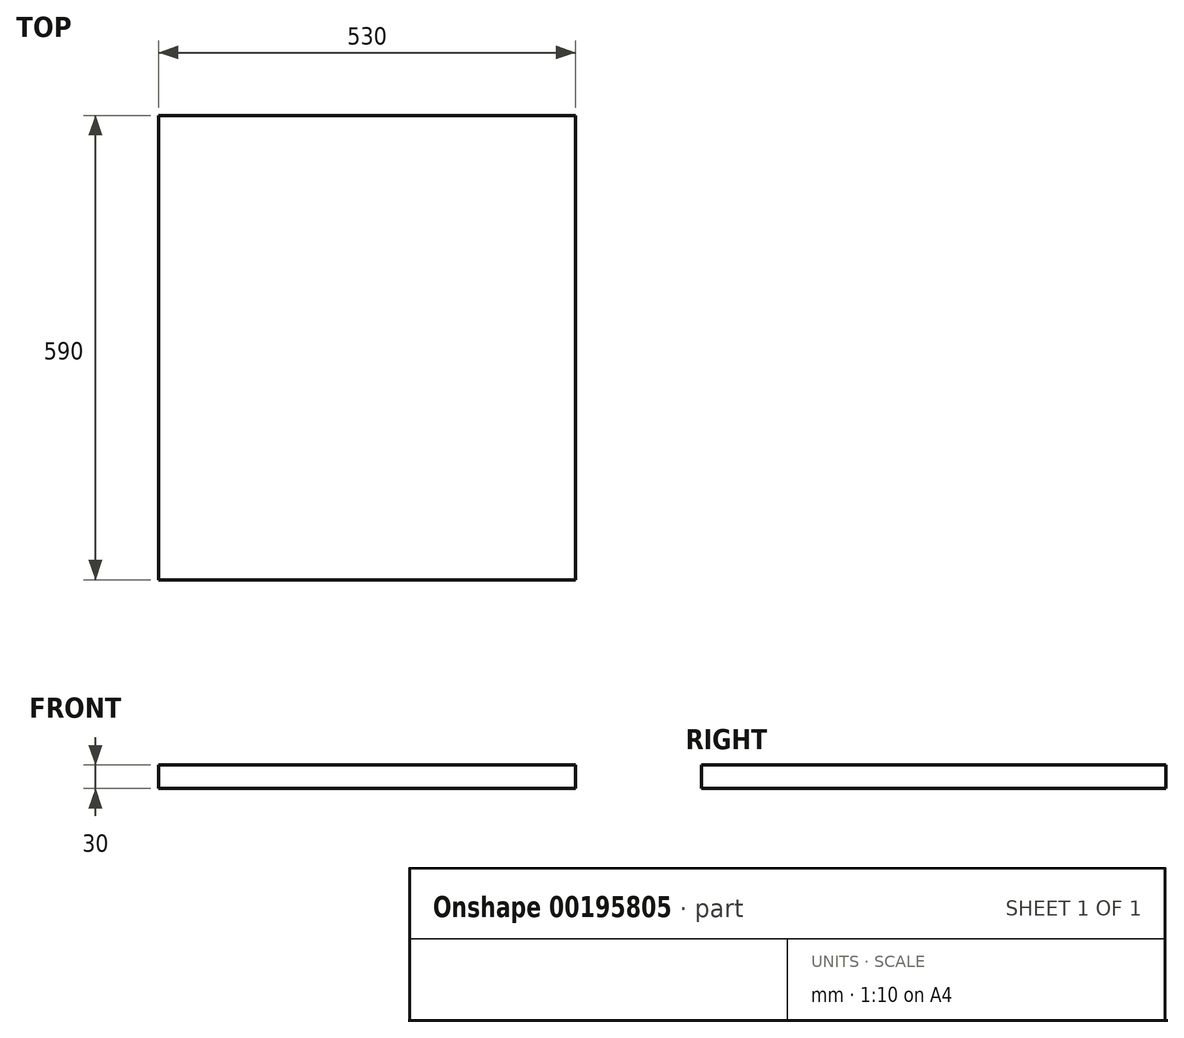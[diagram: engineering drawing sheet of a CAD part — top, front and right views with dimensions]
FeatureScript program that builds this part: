
annotation { "Feature Type Name" : "Feature", "Feature Type Description" : "" }
export const myFeature = defineFeature(function(context is Context, id is Id, definition is map)
    precondition{}
    {
        {
            var Q0;
            Q0=qCreatedBy(makeId("Top.planeOp"),FACE);
            var sketch = newSketch(context, id + "F0", { "sketchPlane" : qUnion([Q0])});
            skLineSegment(sketch, "E0.bottom", {"start": v(-603.57, -364.41) * mm, "end": v(-73.57, -364.41) * mm});
            skLineSegment(sketch, "E0.top", {"start": v(-603.57, 225.59) * mm, "end": v(-73.57, 225.59) * mm});
            skLineSegment(sketch, "E0.left", {"start": v(-603.57, -364.41) * mm, "end": v(-603.57, 225.59) * mm});
            skLineSegment(sketch, "E0.right", {"start": v(-73.57, -364.41) * mm, "end": v(-73.57, 225.59) * mm});
            skSolve(sketch);
        }
        {
            var Q0;
            Q0=makeQuery(id+"F0.imprint","IMPRINT",FACE,{"disambiguationData":[TD([[makeQuery(id+"F0.imprint","IMPRINT",EDGE,{"derivedFrom":sQuery(id+"F0.wireOp",EDGE,"E0.bottom")}),1.0]])]});
            extrude(context, id + "F1", {"entities" : qUnion([Q0]), "depth" : 30 * mm});
        }
    });
